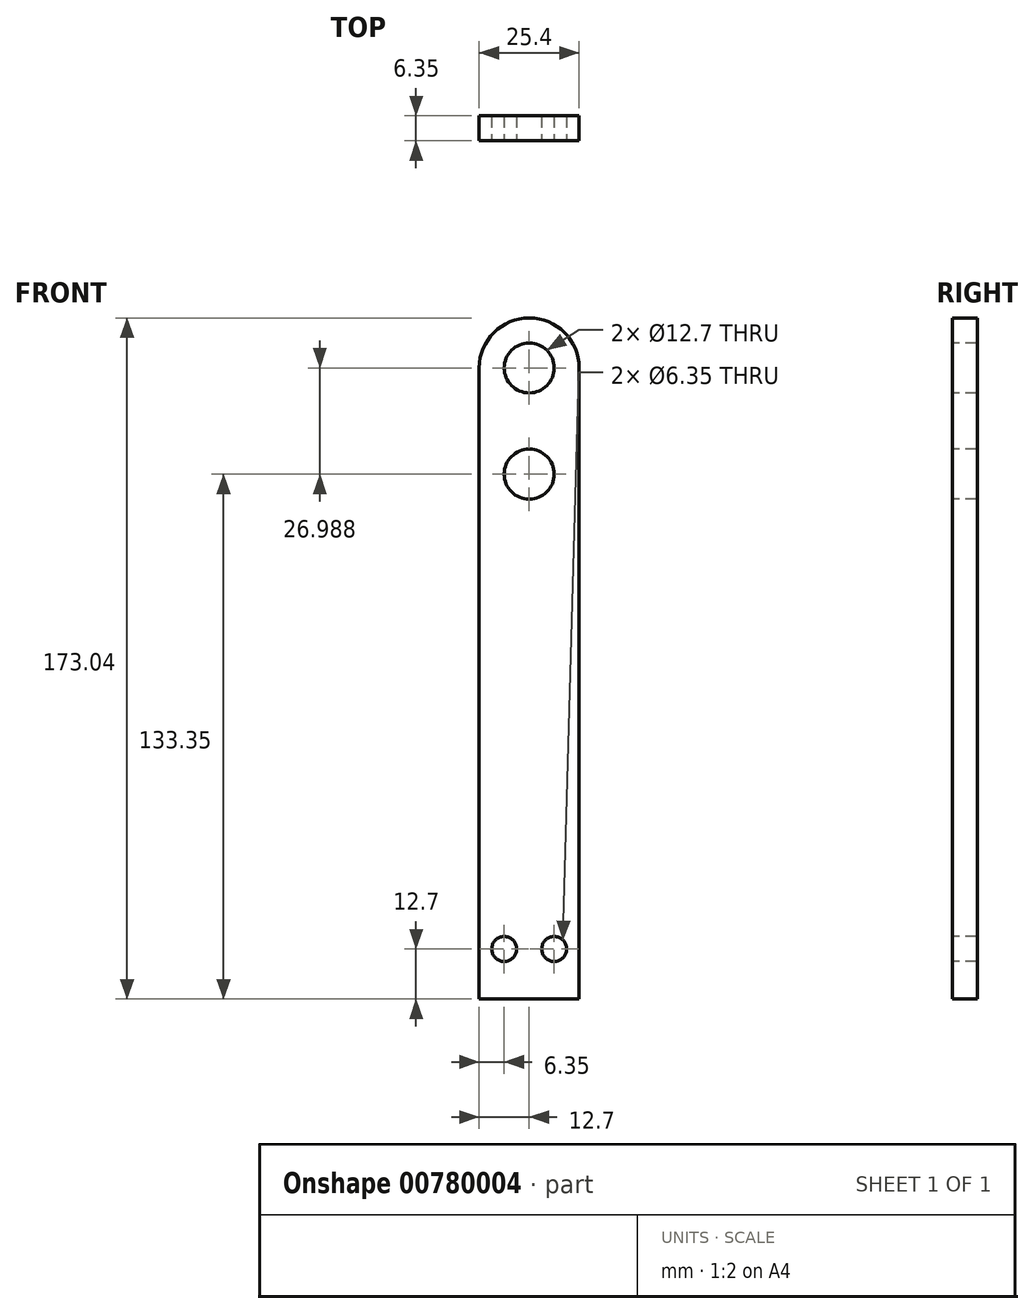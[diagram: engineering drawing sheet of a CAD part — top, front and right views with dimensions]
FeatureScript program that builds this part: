
annotation { "Feature Type Name" : "Feature", "Feature Type Description" : "" }
export const myFeature = defineFeature(function(context is Context, id is Id, definition is map)
    precondition{}
    {
        {
            var Q0;
            Q0=qCreatedBy(makeId("Front.planeOp"),FACE);
            var sketch = newSketch(context, id + "F0", { "sketchPlane" : qUnion([Q0])});
            skLineSegment(sketch, "E0.bottom", {"start": v(0, 0) * mm, "end": v(25.4, 0) * mm});
            skLineSegment(sketch, "E0.left", {"start": v(0, 0) * mm, "end": v(0, 160.34) * mm});
            skLineSegment(sketch, "E0.right", {"start": v(25.4, 0) * mm, "end": v(25.4, 160.34) * mm});
            skArc(sketch, "E1", {"start": v(25.4, 160.34) * mm, "mid": v(12.7, 173.04) * mm, "end": v(0, 160.34) * mm});
            skPoint(sketch, "E1.centerSnap0", {"position": v(12.7, 173.04) * mm});
            skPoint(sketch, "E2.orphan", {"position": v(0, 173.04) * mm});
            skPoint(sketch, "E3.orphan", {"position": v(25.4, 173.04) * mm});
            skSolve(sketch);
        }
        {
            var Q0;
            Q0 = qSketchRegion(id + "F0", true);
            extrude(context, id + "F1", {"entities" : qUnion([Q0]), "depth" : 6.35 * mm, "offsetDistance" : 25.4 * mm});
        }
        {
            var Q0;
            Q0=makeQuery(id+"F1.opExtrude","CAP_FACE",FACE,{"disambiguationData":[OSD([sQuery(id+"F0.wireOp",EDGE,"E0.bottom"),sQuery(id+"F0.wireOp",EDGE,"E0.left"),sQuery(id+"F0.wireOp",EDGE,"E0.right"),sQuery(id+"F0.wireOp",EDGE,"E1")])],"isStart":false});
            var sketch = newSketch(context, id + "F2", { "sketchPlane" : qUnion([Q0])});
            skCircle(sketch, "E4", {"center": v(12.7, 160.34) * mm, "radius": 6.35 * mm});
            skCircle(sketch, "E5", {"center": v(12.7, 133.35) * mm, "radius": 6.35 * mm});
            skLineSegment(sketch, "E6", {"start": v(0, 12.7) * mm, "end": v(25.4, 12.7) * mm, "construction": true});
            skCircle(sketch, "E7", {"center": v(6.35, 12.7) * mm, "radius": 3.18 * mm});
            skCircle(sketch, "E8", {"center": v(19.05, 12.7) * mm, "radius": 3.18 * mm});
            skSolve(sketch);
        }
        {
            var Q0;
            Q0 = qSketchRegion(id + "F2", true);
            extrude(context, id + "F3", {"entities" : qUnion([Q0]), "operationType" : NewBodyOperationType.REMOVE, "oppositeDirection" : true, "depth" : 25.4 * mm, "offsetDistance" : 25.4 * mm});
        }
    });
